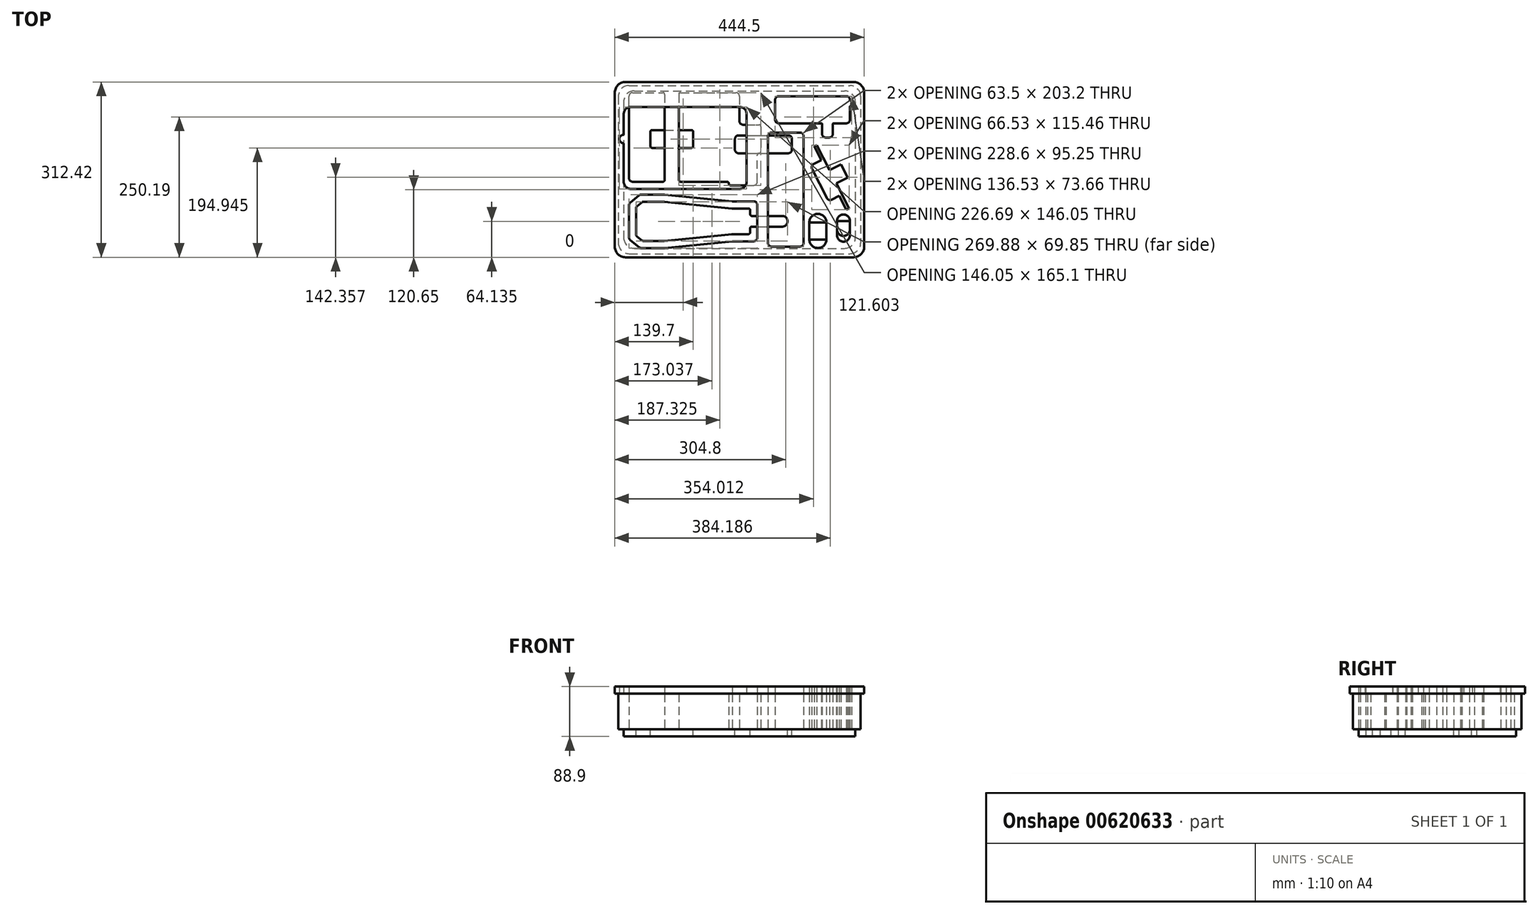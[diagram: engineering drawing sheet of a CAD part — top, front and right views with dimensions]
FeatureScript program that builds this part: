
annotation { "Feature Type Name" : "Feature", "Feature Type Description" : "" }
export const myFeature = defineFeature(function(context is Context, id is Id, definition is map)
    precondition{}
    {
        {
            var Q0;
            Q0=qCreatedBy(makeId("Top.planeOp"),FACE);
            var sketch = newSketch(context, id + "F0", { "sketchPlane" : qUnion([Q0])});
            skLineSegment(sketch, "E0.bottom", {"start": v(-196.85, 149.86) * mm, "end": v(196.85, 149.86) * mm});
            skLineSegment(sketch, "E0.top", {"start": v(-196.85, -149.86) * mm, "end": v(196.85, -149.86) * mm});
            skLineSegment(sketch, "E0.left", {"start": v(-215.9, 130.81) * mm, "end": v(-215.9, -130.81) * mm});
            skLineSegment(sketch, "E0.right", {"start": v(215.9, 130.81) * mm, "end": v(215.9, -130.8) * mm});
            skLineSegment(sketch, "E1.bottom", {"start": v(-196.85, -15.24) * mm, "end": v(-196.85, 130.81) * mm});
            skLineSegment(sketch, "E1.top", {"start": v(31.75, -21.59) * mm, "end": v(31.75, 26.04) * mm});
            skLineSegment(sketch, "E1.right", {"start": v(-190.5, 137.16) * mm, "end": v(-136.52, 137.16) * mm});
            skLineSegment(sketch, "E2.bottom", {"start": v(124.46, -93.98) * mm, "end": v(154.94, -93.98) * mm});
            skLineSegment(sketch, "E2.top", {"start": v(124.46, -124.46) * mm, "end": v(154.94, -124.46) * mm});
            skLineSegment(sketch, "E2.left", {"start": v(124.46, -93.98) * mm, "end": v(124.46, -124.46) * mm});
            skLineSegment(sketch, "E2.right", {"start": v(154.94, -93.98) * mm, "end": v(154.94, -124.46) * mm});
            skLineSegment(sketch, "E3", {"start": v(142.6, -24.8) * mm, "end": v(186.74, -2.32) * mm, "construction": true});
            skLineSegment(sketch, "E4", {"start": v(142.6, -24.8) * mm, "end": v(155.87, -50.83) * mm});
            skLineSegment(sketch, "E5", {"start": v(164.4, -53.6) * mm, "end": v(177.99, -46.7) * mm});
            skLineSegment(sketch, "E6", {"start": v(177.99, -46.7) * mm, "end": v(190.67, -71.59) * mm});
            skLineSegment(sketch, "E7", {"start": v(190.67, -71.59) * mm, "end": v(195.2, -69.28) * mm});
            skLineSegment(sketch, "E8", {"start": v(160.32, -0.82) * mm, "end": v(180.68, 9.56) * mm});
            skLineSegment(sketch, "E9", {"start": v(180.68, 9.56) * mm, "end": v(186.74, -2.32) * mm});
            skPoint(sketch, "E10.visualSharp", {"position": v(158.75, -56.5) * mm});
            skArc(sketch, "E10.filletArc", {"start": v(155.87, -50.83) * mm, "mid": v(159.56, -54) * mm, "end": v(164.4, -53.6) * mm});
            skArc(sketch, "E11.MirrorCS", {"start": v(129.35, 1.22) * mm, "mid": v(128.96, 6.06) * mm, "end": v(132.12, 9.76) * mm});
            skLineSegment(sketch, "E12.MirrorCS", {"start": v(145.7, 16.68) * mm, "end": v(133.02, 41.57) * mm});
            skLineSegment(sketch, "E13.MirrorCS", {"start": v(132.12, 9.76) * mm, "end": v(145.7, 16.68) * mm});
            skPoint(sketch, "E14.MirrorP", {"position": v(126.46, 6.88) * mm});
            skLineSegment(sketch, "E15.MirrorCS", {"start": v(172.42, -24.58) * mm, "end": v(192.8, -14.2) * mm});
            skLineSegment(sketch, "E16.MirrorCS", {"start": v(142.6, -24.8) * mm, "end": v(129.35, 1.22) * mm});
            skLineSegment(sketch, "E17.MirrorCS", {"start": v(192.8, -14.2) * mm, "end": v(186.74, -2.32) * mm});
            skLineSegment(sketch, "E18", {"start": v(172.42, -24.58) * mm, "end": v(195.2, -69.28) * mm});
            skPoint(sketch, "E19.visualSharp", {"position": v(-215.9, 149.86) * mm});
            skArc(sketch, "E19.filletArc", {"start": v(-196.85, 149.86) * mm, "mid": v(-210.32, 144.28) * mm, "end": v(-215.9, 130.81) * mm});
            skPoint(sketch, "E20.visualSharp", {"position": v(215.9, 149.86) * mm});
            skArc(sketch, "E20.filletArc", {"start": v(215.9, 130.81) * mm, "mid": v(210.32, 144.28) * mm, "end": v(196.85, 149.86) * mm});
            skPoint(sketch, "E21.visualSharp", {"position": v(215.9, -149.86) * mm});
            skArc(sketch, "E21.filletArc", {"start": v(196.85, -149.86) * mm, "mid": v(210.32, -144.28) * mm, "end": v(215.9, -130.8) * mm});
            skPoint(sketch, "E22.visualSharp", {"position": v(-215.9, -149.86) * mm});
            skArc(sketch, "E22.filletArc", {"start": v(-215.9, -130.81) * mm, "mid": v(-210.32, -144.28) * mm, "end": v(-196.85, -149.86) * mm});
            skPoint(sketch, "E23.visualSharp", {"position": v(-196.85, -27.94) * mm});
            skPoint(sketch, "E24.visualSharp", {"position": v(31.75, -27.94) * mm});
            skArc(sketch, "E24.filletArc", {"start": v(25.4, -27.94) * mm, "mid": v(29.9, -26.08) * mm, "end": v(31.75, -21.59) * mm});
            skPoint(sketch, "E25.visualSharp", {"position": v(-196.85, 137.16) * mm});
            skArc(sketch, "E25.filletArc", {"start": v(-190.5, 137.16) * mm, "mid": v(-195, 135.3) * mm, "end": v(-196.85, 130.81) * mm});
            skPoint(sketch, "E26.visualSharp", {"position": v(31.75, 137.16) * mm});
            skArc(sketch, "E26.filletArc", {"start": v(31.75, 130.81) * mm, "mid": v(29.9, 135.3) * mm, "end": v(25.4, 137.16) * mm, "construction": true});
            skLineSegment(sketch, "E27.bottom", {"start": v(63.5, 88.9) * mm, "end": v(63.5, 124.46) * mm});
            skLineSegment(sketch, "E27.top", {"start": v(196.85, 88.9) * mm, "end": v(196.85, 112.08) * mm});
            skLineSegment(sketch, "E27.left", {"start": v(69.85, 82.55) * mm, "end": v(146.05, 82.55) * mm});
            skLineSegment(sketch, "E27.right", {"start": v(69.85, 130.81) * mm, "end": v(190.5, 130.81) * mm});
            skLineSegment(sketch, "E28.bottom", {"start": v(147.32, 81.28) * mm, "end": v(147.32, 63.5) * mm});
            skLineSegment(sketch, "E28.top", {"start": v(166.37, 81.28) * mm, "end": v(166.37, 63.5) * mm});
            skLineSegment(sketch, "E28.right", {"start": v(153.67, 57.15) * mm, "end": v(160.02, 57.15) * mm});
            skLineSegment(sketch, "E29.trimOffspring", {"start": v(167.64, 82.55) * mm, "end": v(190.5, 82.55) * mm});
            skLineSegment(sketch, "E30", {"start": v(147.32, 82.55) * mm, "end": v(166.37, 82.55) * mm, "construction": true});
            skPoint(sketch, "E31.visualSharp", {"position": v(63.5, 82.55) * mm});
            skArc(sketch, "E31.filletArc", {"start": v(63.5, 88.9) * mm, "mid": v(65.36, 84.4) * mm, "end": v(69.85, 82.55) * mm});
            skPoint(sketch, "E32.visualSharp", {"position": v(196.85, 82.55) * mm});
            skArc(sketch, "E32.filletArc", {"start": v(190.5, 82.55) * mm, "mid": v(195, 84.4) * mm, "end": v(196.85, 88.9) * mm});
            skArc(sketch, "E33.filletArc", {"start": v(196.85, 124.46) * mm, "mid": v(195, 128.95) * mm, "end": v(190.5, 130.81) * mm});
            skPoint(sketch, "E34.visualSharp", {"position": v(63.5, 130.81) * mm});
            skArc(sketch, "E34.filletArc", {"start": v(69.85, 130.81) * mm, "mid": v(65.36, 128.95) * mm, "end": v(63.5, 124.46) * mm});
            skPoint(sketch, "E35.visualSharp", {"position": v(147.32, 57.15) * mm});
            skArc(sketch, "E35.filletArc", {"start": v(147.32, 63.5) * mm, "mid": v(149.18, 59) * mm, "end": v(153.67, 57.15) * mm});
            skPoint(sketch, "E36.visualSharp", {"position": v(166.37, 57.15) * mm});
            skArc(sketch, "E36.filletArc", {"start": v(160.02, 57.15) * mm, "mid": v(164.51, 59) * mm, "end": v(166.37, 63.5) * mm});
            skLineSegment(sketch, "E37.bottom", {"start": v(173.74, -91.44) * mm, "end": v(196.85, -91.44) * mm});
            skLineSegment(sketch, "E37.left", {"start": v(173.74, -91.44) * mm, "end": v(173.74, -106.68) * mm});
            skLineSegment(sketch, "E37.right", {"start": v(196.85, -91.44) * mm, "end": v(196.85, -106.68) * mm});
            skArc(sketch, "E38", {"start": v(173.74, -106.68) * mm, "mid": v(185.3, -118.24) * mm, "end": v(196.85, -106.68) * mm});
            skLineSegment(sketch, "E39.bottom", {"start": v(-196.85, -139.7) * mm, "end": v(-196.85, -44.45) * mm, "construction": true});
            skLineSegment(sketch, "E39.top", {"start": v(31.75, -139.7) * mm, "end": v(31.75, -44.45) * mm, "construction": true});
            skLineSegment(sketch, "E39.left", {"start": v(-196.85, -139.7) * mm, "end": v(31.75, -139.7) * mm, "construction": true});
            skLineSegment(sketch, "E39.right", {"start": v(-196.85, -44.45) * mm, "end": v(31.75, -44.45) * mm, "construction": true});
            skLineSegment(sketch, "E40", {"start": v(-196.85, -92.08) * mm, "end": v(31.75, -92.07) * mm, "construction": true});
            skLineSegment(sketch, "E41", {"start": v(-196.85, -123.83) * mm, "end": v(31.75, -123.82) * mm, "construction": true});
            skLineSegment(sketch, "E42.MirrorCS", {"start": v(-196.85, -60.33) * mm, "end": v(31.75, -60.32) * mm, "construction": true});
            skLineSegment(sketch, "E43", {"start": v(-196.85, -127.64) * mm, "end": v(31.75, -127.63) * mm, "construction": true});
            skLineSegment(sketch, "E44.MirrorCS", {"start": v(-196.85, -56.51) * mm, "end": v(31.75, -56.51) * mm, "construction": true});
            skLineSegment(sketch, "E45", {"start": v(-177.16, -139.7) * mm, "end": v(-177.16, -44.45) * mm, "construction": true});
            skLineSegment(sketch, "E46", {"start": v(-133.35, -139.7) * mm, "end": v(-133.35, -44.45) * mm, "construction": true});
            skLineSegment(sketch, "E47", {"start": v(-12.7, -139.7) * mm, "end": v(-12.7, -44.45) * mm, "construction": true});
            skLineSegment(sketch, "E48", {"start": v(-196.85, -120.79) * mm, "end": v(-196.85, -63.36) * mm});
            skLineSegment(sketch, "E49", {"start": v(-194.49, -58.42) * mm, "end": v(-178.9, -45.86) * mm});
            skLineSegment(sketch, "E50", {"start": v(-174.92, -44.45) * mm, "end": v(-133.35, -44.45) * mm});
            skLineSegment(sketch, "E51", {"start": v(-133.35, -44.45) * mm, "end": v(-12.7, -56.51) * mm});
            skLineSegment(sketch, "E52", {"start": v(-12.7, -56.51) * mm, "end": v(25.4, -56.51) * mm});
            skLineSegment(sketch, "E53", {"start": v(31.75, -62.86) * mm, "end": v(31.75, -121.28) * mm});
            skLineSegment(sketch, "E54", {"start": v(25.4, -127.63) * mm, "end": v(-12.7, -127.63) * mm});
            skLineSegment(sketch, "E55", {"start": v(-12.7, -127.64) * mm, "end": v(-133.35, -139.7) * mm});
            skLineSegment(sketch, "E56", {"start": v(-133.35, -139.7) * mm, "end": v(-174.92, -139.7) * mm});
            skLineSegment(sketch, "E57", {"start": v(-178.9, -138.3) * mm, "end": v(-194.49, -125.73) * mm});
            skPoint(sketch, "E58.visualSharp", {"position": v(31.75, -127.64) * mm});
            skArc(sketch, "E58.filletArc", {"start": v(25.4, -127.63) * mm, "mid": v(29.9, -125.78) * mm, "end": v(31.75, -121.28) * mm});
            skPoint(sketch, "E59.visualSharp", {"position": v(31.75, -56.51) * mm});
            skArc(sketch, "E59.filletArc", {"start": v(31.75, -62.86) * mm, "mid": v(29.9, -58.37) * mm, "end": v(25.4, -56.51) * mm});
            skPoint(sketch, "E60.visualSharp", {"position": v(-196.85, -123.83) * mm});
            skArc(sketch, "E60.filletArc", {"start": v(-196.85, -120.79) * mm, "mid": v(-196.23, -123.53) * mm, "end": v(-194.49, -125.73) * mm});
            skPoint(sketch, "E61.visualSharp", {"position": v(-177.16, -139.7) * mm});
            skArc(sketch, "E61.filletArc", {"start": v(-178.9, -138.3) * mm, "mid": v(-177.04, -139.34) * mm, "end": v(-174.92, -139.7) * mm});
            skPoint(sketch, "E62.visualSharp", {"position": v(-196.85, -60.33) * mm});
            skArc(sketch, "E62.filletArc", {"start": v(-194.49, -58.42) * mm, "mid": v(-196.23, -60.62) * mm, "end": v(-196.85, -63.36) * mm});
            skPoint(sketch, "E63.visualSharp", {"position": v(-177.16, -44.45) * mm});
            skArc(sketch, "E63.filletArc", {"start": v(-174.92, -44.45) * mm, "mid": v(-177.04, -44.81) * mm, "end": v(-178.9, -45.86) * mm});
            skLineSegment(sketch, "E64", {"start": v(173.74, -106.68) * mm, "end": v(196.85, -106.68) * mm, "construction": true});
            skLineSegment(sketch, "E65.MirrorCS", {"start": v(160.32, -0.82) * mm, "end": v(137.54, 43.88) * mm});
            skLineSegment(sketch, "E66.MirrorCS", {"start": v(133.02, 41.57) * mm, "end": v(137.54, 43.88) * mm});
            skLineSegment(sketch, "E67", {"start": v(198.12, 122.87) * mm, "end": v(198.76, 122.87) * mm});
            skLineSegment(sketch, "E68", {"start": v(200.02, 121.6) * mm, "end": v(200.02, 114.62) * mm});
            skLineSegment(sketch, "E69", {"start": v(198.76, 113.35) * mm, "end": v(198.12, 113.35) * mm});
            skPoint(sketch, "E70.visualSharp", {"position": v(166.37, 82.55) * mm});
            skArc(sketch, "E70.filletArc", {"start": v(167.64, 82.55) * mm, "mid": v(166.74, 82.18) * mm, "end": v(166.37, 81.28) * mm});
            skPoint(sketch, "E71.visualSharp", {"position": v(147.32, 82.55) * mm});
            skArc(sketch, "E71.filletArc", {"start": v(147.32, 81.28) * mm, "mid": v(146.95, 82.18) * mm, "end": v(146.05, 82.55) * mm});
            skPoint(sketch, "E72.visualSharp", {"position": v(200.03, 113.35) * mm});
            skArc(sketch, "E72.filletArc", {"start": v(198.76, 113.35) * mm, "mid": v(199.65, 113.72) * mm, "end": v(200.03, 114.62) * mm});
            skPoint(sketch, "E73.visualSharp", {"position": v(200.03, 122.87) * mm});
            skArc(sketch, "E73.filletArc", {"start": v(200.02, 121.6) * mm, "mid": v(199.65, 122.5) * mm, "end": v(198.76, 122.87) * mm});
            skPoint(sketch, "E74.visualSharp", {"position": v(196.85, 122.87) * mm});
            skArc(sketch, "E74.filletArc", {"start": v(196.85, 124.13) * mm, "mid": v(197.23, 123.24) * mm, "end": v(198.12, 122.87) * mm});
            skPoint(sketch, "E75.visualSharp", {"position": v(196.85, 113.35) * mm});
            skArc(sketch, "E75.filletArc", {"start": v(198.12, 113.35) * mm, "mid": v(197.22, 112.98) * mm, "end": v(196.85, 112.08) * mm});
            skLineSegment(sketch, "E76", {"start": v(-196.85, 54.61) * mm, "end": v(31.75, 54.61) * mm, "construction": true});
            skLineSegment(sketch, "E77", {"start": v(-82.55, -27.94) * mm, "end": v(-82.55, 137.16) * mm, "construction": true});
            skLineSegment(sketch, "E78", {"start": v(0, 149.86) * mm, "end": v(0, -149.86) * mm, "construction": true});
            skLineSegment(sketch, "E79", {"start": v(-215.9, 0) * mm, "end": v(215.9, 0) * mm, "construction": true});
            skPoint(sketch, "E80", {"position": v(0, 0) * mm});
            skPoint(sketch, "E81", {"position": v(-82.55, 54.61) * mm});
            skPoint(sketch, "E82", {"position": v(-133.35, -92.08) * mm});
            skLineSegment(sketch, "E83", {"start": v(63.5, 106.68) * mm, "end": v(196.85, 106.68) * mm, "construction": true});
            skLineSegment(sketch, "E84", {"start": v(130.18, 130.81) * mm, "end": v(130.18, 82.55) * mm, "construction": true});
            skPoint(sketch, "E85", {"position": v(130.18, 106.68) * mm});
            skLineSegment(sketch, "E86", {"start": v(172.42, -24.58) * mm, "end": v(160.32, -0.82) * mm, "construction": true});
            skPoint(sketch, "E87", {"position": v(166.37, -12.7) * mm});
            skLineSegment(sketch, "E88", {"start": v(196.85, 124.46) * mm, "end": v(196.85, 124.13) * mm});
            skLineSegment(sketch, "E89", {"start": v(196.85, 124.13) * mm, "end": v(196.85, 112.08) * mm, "construction": true});
            skArc(sketch, "E90", {"start": v(31.75, -21.59) * mm, "mid": v(29.9, -26.08) * mm, "end": v(25.4, -27.94) * mm});
            skLineSegment(sketch, "E91.bottom", {"start": v(107.95, -137.16) * mm, "end": v(57.15, -137.16) * mm});
            skLineSegment(sketch, "E91.top", {"start": v(107.95, 66.04) * mm, "end": v(57.15, 66.04) * mm});
            skLineSegment(sketch, "E91.left", {"start": v(114.3, -130.8) * mm, "end": v(114.3, 59.7) * mm});
            skLineSegment(sketch, "E91.right", {"start": v(50.8, -130.8) * mm, "end": v(50.8, 59.7) * mm});
            skLineSegment(sketch, "E92", {"start": v(82.55, -137.16) * mm, "end": v(82.55, 66.04) * mm, "construction": true});
            skLineSegment(sketch, "E93", {"start": v(114.3, -35.56) * mm, "end": v(50.8, -35.56) * mm, "construction": true});
            skPoint(sketch, "E94", {"position": v(82.55, -35.56) * mm});
            skPoint(sketch, "E95.visualSharp", {"position": v(114.3, -137.16) * mm});
            skArc(sketch, "E95.filletArc", {"start": v(107.95, -137.16) * mm, "mid": v(112.44, -135.3) * mm, "end": v(114.3, -130.8) * mm});
            skPoint(sketch, "E96.visualSharp", {"position": v(50.8, -137.16) * mm});
            skArc(sketch, "E96.filletArc", {"start": v(50.8, -130.8) * mm, "mid": v(52.66, -135.3) * mm, "end": v(57.15, -137.16) * mm});
            skPoint(sketch, "E97.visualSharp", {"position": v(50.8, 66.04) * mm});
            skArc(sketch, "E97.filletArc", {"start": v(57.15, 66.04) * mm, "mid": v(52.66, 64.18) * mm, "end": v(50.8, 59.7) * mm});
            skPoint(sketch, "E98.visualSharp", {"position": v(114.3, 66.04) * mm});
            skArc(sketch, "E98.filletArc", {"start": v(114.3, 59.7) * mm, "mid": v(112.44, 64.18) * mm, "end": v(107.95, 66.04) * mm});
            skLineSegment(sketch, "E99.left", {"start": v(-107.95, 133.99) * mm, "end": v(-107.95, -18.41) * mm});
            skLineSegment(sketch, "E99.right", {"start": v(-133.35, 133.99) * mm, "end": v(-133.35, -18.41) * mm});
            skLineSegment(sketch, "E100", {"start": v(34.93, 80.01) * mm, "end": v(34.92, 80.01) * mm});
            skLineSegment(sketch, "E101.MirrorCS", {"start": v(34.93, 29.21) * mm, "end": v(34.93, 29.21) * mm});
            skLineSegment(sketch, "E102", {"start": v(38.1, 76.84) * mm, "end": v(38.1, 32.39) * mm});
            skLineSegment(sketch, "E103", {"start": v(-104.77, 137.16) * mm, "end": v(-6.35, 137.16) * mm});
            skLineSegment(sketch, "E104", {"start": v(31.75, 83.19) * mm, "end": v(31.75, 130.81) * mm, "construction": true});
            skLineSegment(sketch, "E105", {"start": v(31.75, 29.21) * mm, "end": v(31.75, 80.01) * mm, "construction": true});
            skLineSegment(sketch, "E106", {"start": v(-133.35, 137.16) * mm, "end": v(-107.95, 137.16) * mm, "construction": true});
            skPoint(sketch, "E107.visualSharp", {"position": v(-107.95, 137.16) * mm});
            skArc(sketch, "E107.filletArc", {"start": v(-104.77, 137.16) * mm, "mid": v(-107.02, 136.23) * mm, "end": v(-107.95, 133.99) * mm});
            skPoint(sketch, "E108.visualSharp", {"position": v(-133.35, 137.16) * mm});
            skArc(sketch, "E108.filletArc", {"start": v(-133.35, 133.99) * mm, "mid": v(-134.28, 136.23) * mm, "end": v(-136.52, 137.16) * mm});
            skPoint(sketch, "E109.visualSharp", {"position": v(31.75, 80.01) * mm});
            skPoint(sketch, "E110.visualSharp", {"position": v(31.75, 29.21) * mm});
            skArc(sketch, "E110.filletArc", {"start": v(34.93, 29.21) * mm, "mid": v(32.68, 28.28) * mm, "end": v(31.75, 26.04) * mm});
            skPoint(sketch, "E111.visualSharp", {"position": v(38.1, 29.21) * mm});
            skArc(sketch, "E111.filletArc", {"start": v(34.93, 29.21) * mm, "mid": v(37.17, 30.14) * mm, "end": v(38.1, 32.39) * mm});
            skPoint(sketch, "E112.visualSharp", {"position": v(38.1, 80.01) * mm});
            skArc(sketch, "E112.filletArc", {"start": v(38.1, 76.84) * mm, "mid": v(37.17, 79.08) * mm, "end": v(34.92, 80.01) * mm});
            skLineSegment(sketch, "E113", {"start": v(0, 130.81) * mm, "end": v(0, 86.36) * mm});
            skLineSegment(sketch, "E114", {"start": v(6.35, 80.01) * mm, "end": v(34.93, 80.01) * mm});
            skPoint(sketch, "E115.visualSharp", {"position": v(0, 80.01) * mm});
            skArc(sketch, "E115.filletArc", {"start": v(0, 86.36) * mm, "mid": v(1.86, 81.87) * mm, "end": v(6.35, 80.01) * mm});
            skLineSegment(sketch, "E116", {"start": v(-6.35, 137.16) * mm, "end": v(0, 137.16) * mm, "construction": true});
            skLineSegment(sketch, "E117", {"start": v(0, 137.16) * mm, "end": v(25.4, 137.16) * mm, "construction": true});
            skPoint(sketch, "E118.visualSharp", {"position": v(0, 137.16) * mm});
            skArc(sketch, "E118.filletArc", {"start": v(0, 130.81) * mm, "mid": v(-1.86, 135.3) * mm, "end": v(-6.35, 137.16) * mm});
            skLineSegment(sketch, "E119", {"start": v(-6.35, 137.16) * mm, "end": v(-6.35, 137.16) * mm});
            skLineSegment(sketch, "E120", {"start": v(-19.05, -24.76) * mm, "end": v(-19.05, -24.76) * mm});
            skLineSegment(sketch, "E121", {"start": v(-22.22, -21.59) * mm, "end": v(-104.78, -21.59) * mm});
            skLineSegment(sketch, "E122", {"start": v(-133.35, -21.59) * mm, "end": v(-133.35, -24.76) * mm, "construction": true});
            skLineSegment(sketch, "E123", {"start": v(-15.88, -27.94) * mm, "end": v(25.4, -27.94) * mm});
            skLineSegment(sketch, "E124", {"start": v(-107.95, -21.59) * mm, "end": v(-107.95, -24.76) * mm, "construction": true});
            skPoint(sketch, "E125.visualSharp", {"position": v(-196.85, -21.59) * mm});
            skArc(sketch, "E125.filletArc", {"start": v(-196.85, -15.24) * mm, "mid": v(-195, -19.73) * mm, "end": v(-190.5, -21.59) * mm});
            skPoint(sketch, "E126.visualSharp", {"position": v(-19.05, -21.59) * mm});
            skArc(sketch, "E126.filletArc", {"start": v(-19.05, -24.76) * mm, "mid": v(-19.98, -22.52) * mm, "end": v(-22.22, -21.59) * mm});
            skPoint(sketch, "E127.visualSharp", {"position": v(-19.05, -27.94) * mm});
            skArc(sketch, "E127.filletArc", {"start": v(-19.05, -24.76) * mm, "mid": v(-18.12, -27.01) * mm, "end": v(-15.88, -27.94) * mm});
            skLineSegment(sketch, "E128", {"start": v(-136.53, -21.59) * mm, "end": v(-190.5, -21.59) * mm});
            skPoint(sketch, "E129.visualSharp", {"position": v(-133.35, -21.59) * mm});
            skArc(sketch, "E129.filletArc", {"start": v(-136.53, -21.59) * mm, "mid": v(-134.28, -20.66) * mm, "end": v(-133.35, -18.41) * mm});
            skPoint(sketch, "E130.visualSharp", {"position": v(-107.95, -21.59) * mm});
            skArc(sketch, "E130.filletArc", {"start": v(-107.95, -18.41) * mm, "mid": v(-107.02, -20.66) * mm, "end": v(-104.78, -21.59) * mm});
            skSolve(sketch);
        }
        {
            var Q0;
            Q0=qSketchRegion(id+"F0",true);
            extrude(context, id + "F1", {"entities" : qUnion([Q0]), "depth" : 63.5 * mm, "offsetDistance" : 25.4 * mm});
        }
        {
            var Q0;
            Q0=qCreatedBy(makeId("Top.planeOp"),FACE);
            var sketch = newSketch(context, id + "F2", { "sketchPlane" : qUnion([Q0])});
            skLineSegment(sketch, "E131.0", {"start": v(-215.9, 149.86) * mm, "end": v(215.9, 149.86) * mm, "construction": true});
            skLineSegment(sketch, "E132.0", {"start": v(-215.9, 149.86) * mm, "end": v(-215.9, -149.86) * mm, "construction": true});
            skLineSegment(sketch, "E133.0", {"start": v(215.9, 149.86) * mm, "end": v(215.9, -149.86) * mm, "construction": true});
            skLineSegment(sketch, "E134.0", {"start": v(-190.26, -149.86) * mm, "end": v(215.9, -149.86) * mm, "construction": true});
            skPoint(sketch, "E135.orphan", {"position": v(-196.85, 149.86) * mm});
            skPoint(sketch, "E136.orphan", {"position": v(-215.9, 130.81) * mm});
            skPoint(sketch, "E137.orphan", {"position": v(196.85, 149.86) * mm});
            skPoint(sketch, "E138.orphan", {"position": v(215.9, 130.81) * mm});
            skPoint(sketch, "E139.orphan", {"position": v(215.9, -130.8) * mm});
            skPoint(sketch, "E140.orphan", {"position": v(196.85, -149.86) * mm});
            skPoint(sketch, "E141.orphan", {"position": v(-196.85, -149.86) * mm});
            skPoint(sketch, "E142.orphan", {"position": v(-215.9, -130.81) * mm});
            skPoint(sketch, "E143", {"position": v(0, 0) * mm});
            skLineSegment(sketch, "E144", {"start": v(0, 149.86) * mm, "end": v(0, -149.86) * mm, "construction": true});
            skPoint(sketch, "E144.startSnap0", {"position": v(0, 149.86) * mm});
            skLineSegment(sketch, "E145", {"start": v(-215.9, 0) * mm, "end": v(215.9, 0) * mm, "construction": true});
            skLineSegment(sketch, "E146.bottom", {"start": v(-187.32, 140.34) * mm, "end": v(187.33, 140.34) * mm});
            skLineSegment(sketch, "E146.top", {"start": v(-187.33, -140.33) * mm, "end": v(187.32, -140.33) * mm});
            skLineSegment(sketch, "E146.left", {"start": v(-206.38, 121.29) * mm, "end": v(-206.38, -121.28) * mm});
            skLineSegment(sketch, "E146.right", {"start": v(206.38, 121.29) * mm, "end": v(206.38, -121.28) * mm});
            skPoint(sketch, "E147.visualSharp", {"position": v(-206.38, 140.34) * mm});
            skPoint(sketch, "E148.visualSharp", {"position": v(206.38, 140.34) * mm});
            skPoint(sketch, "E149.visualSharp", {"position": v(206.38, -140.33) * mm});
            skPoint(sketch, "E150.visualSharp", {"position": v(-206.38, -140.33) * mm});
            skLineSegment(sketch, "E151.0.0", {"start": v(-12.7, -127.63) * mm, "end": v(25.4, -127.63) * mm, "construction": true});
            skArc(sketch, "E151.0.1", {"start": v(25.4, -127.63) * mm, "mid": v(29.9, -125.78) * mm, "end": v(31.75, -121.28) * mm, "construction": true});
            skLineSegment(sketch, "E151.0.2", {"start": v(31.75, -121.28) * mm, "end": v(31.75, -62.86) * mm, "construction": true});
            skArc(sketch, "E151.0.3", {"start": v(31.75, -62.86) * mm, "mid": v(29.9, -58.37) * mm, "end": v(25.4, -56.51) * mm, "construction": true});
            skLineSegment(sketch, "E151.0.4", {"start": v(25.4, -56.51) * mm, "end": v(-12.7, -56.51) * mm, "construction": true});
            skLineSegment(sketch, "E151.0.5", {"start": v(-12.7, -56.52) * mm, "end": v(-133.35, -44.45) * mm, "construction": true});
            skLineSegment(sketch, "E151.0.6", {"start": v(-133.35, -44.45) * mm, "end": v(-174.92, -44.45) * mm, "construction": true});
            skArc(sketch, "E151.0.7", {"start": v(-174.92, -44.45) * mm, "mid": v(-177.04, -44.81) * mm, "end": v(-178.9, -45.86) * mm, "construction": true});
            skLineSegment(sketch, "E151.0.8", {"start": v(-178.9, -45.86) * mm, "end": v(-194.49, -58.42) * mm, "construction": true});
            skArc(sketch, "E151.0.9", {"start": v(-194.49, -58.42) * mm, "mid": v(-196.23, -60.62) * mm, "end": v(-196.85, -63.36) * mm, "construction": true});
            skLineSegment(sketch, "E151.0.10", {"start": v(-196.85, -63.36) * mm, "end": v(-196.85, -120.79) * mm, "construction": true});
            skArc(sketch, "E151.0.11", {"start": v(-196.85, -120.79) * mm, "mid": v(-196.23, -123.53) * mm, "end": v(-194.49, -125.73) * mm, "construction": true});
            skLineSegment(sketch, "E151.0.12", {"start": v(-194.49, -125.73) * mm, "end": v(-178.9, -138.3) * mm, "construction": true});
            skArc(sketch, "E151.0.13", {"start": v(-178.9, -138.3) * mm, "mid": v(-177.04, -139.34) * mm, "end": v(-174.92, -139.7) * mm, "construction": true});
            skLineSegment(sketch, "E151.0.14", {"start": v(-174.92, -139.7) * mm, "end": v(-133.35, -139.7) * mm, "construction": true});
            skLineSegment(sketch, "E151.0.15", {"start": v(-133.35, -139.7) * mm, "end": v(-12.7, -127.64) * mm, "construction": true});
            skArc(sketch, "E152.filletArc", {"start": v(-187.32, 140.34) * mm, "mid": v(-200.8, 134.76) * mm, "end": v(-206.38, 121.29) * mm});
            skArc(sketch, "E153.filletArc", {"start": v(206.38, 121.29) * mm, "mid": v(200.8, 134.76) * mm, "end": v(187.33, 140.34) * mm});
            skArc(sketch, "E154.filletArc", {"start": v(187.32, -140.33) * mm, "mid": v(200.8, -134.76) * mm, "end": v(206.37, -121.28) * mm});
            skArc(sketch, "E155.filletArc", {"start": v(-206.38, -121.28) * mm, "mid": v(-200.8, -134.76) * mm, "end": v(-187.33, -140.33) * mm});
            skLineSegment(sketch, "E156.0", {"start": v(-173.55, -57.85) * mm, "end": v(-182.97, -65.45) * mm});
            skLineSegment(sketch, "E156.1", {"start": v(-134.14, -57.15) * mm, "end": v(-171.56, -57.15) * mm});
            skLineSegment(sketch, "E156.2", {"start": v(-184.15, -67.92) * mm, "end": v(-184.15, -116.23) * mm});
            skLineSegment(sketch, "E156.3", {"start": v(-13.5, -69.2) * mm, "end": v(-133.83, -57.17) * mm});
            skLineSegment(sketch, "E156.4", {"start": v(15.88, -69.21) * mm, "end": v(-13.18, -69.21) * mm});
            skLineSegment(sketch, "E156.5", {"start": v(19.05, -111.76) * mm, "end": v(19.05, -104.78) * mm});
            skLineSegment(sketch, "E156.6", {"start": v(-182.97, -118.7) * mm, "end": v(-173.55, -126.3) * mm});
            skLineSegment(sketch, "E156.7", {"start": v(-171.56, -127) * mm, "end": v(-134.14, -127) * mm});
            skLineSegment(sketch, "E156.8", {"start": v(-133.83, -126.98) * mm, "end": v(-13.5, -114.95) * mm});
            skLineSegment(sketch, "E156.9", {"start": v(-13.18, -114.93) * mm, "end": v(15.88, -114.93) * mm});
            skLineSegment(sketch, "E157", {"start": v(22.23, -82.55) * mm, "end": v(76.2, -82.55) * mm});
            skLineSegment(sketch, "E158", {"start": v(-184.15, -92.08) * mm, "end": v(76.2, -92.08) * mm, "construction": true});
            skLineSegment(sketch, "E159", {"start": v(76.2, -82.55) * mm, "end": v(76.2, -92.08) * mm, "construction": true});
            skLineSegment(sketch, "E160.MirrorCS", {"start": v(22.23, -101.6) * mm, "end": v(76.2, -101.6) * mm});
            skLineSegment(sketch, "E161.MirrorCS", {"start": v(76.2, -101.6) * mm, "end": v(76.2, -92.08) * mm, "construction": true});
            skLineSegment(sketch, "E162", {"start": v(19.05, -79.37) * mm, "end": v(19.05, -72.39) * mm});
            skPoint(sketch, "E163.orphan", {"position": v(19.05, -92.08) * mm});
            skArc(sketch, "E164", {"start": v(76.2, -82.55) * mm, "mid": v(85.73, -92.08) * mm, "end": v(76.2, -101.6) * mm});
            skLineSegment(sketch, "E165.bottom", {"start": v(-1.78, 60.96) * mm, "end": v(87.12, 60.96) * mm});
            skLineSegment(sketch, "E165.top", {"start": v(-1.78, 29.21) * mm, "end": v(87.12, 29.21) * mm});
            skLineSegment(sketch, "E165.left", {"start": v(-8.13, 54.61) * mm, "end": v(-8.13, 35.56) * mm});
            skLineSegment(sketch, "E165.right", {"start": v(93.47, 54.61) * mm, "end": v(93.47, 35.56) * mm});
            skPoint(sketch, "E166.visualSharp", {"position": v(-8.13, 60.96) * mm});
            skArc(sketch, "E166.filletArc", {"start": v(-1.78, 60.96) * mm, "mid": v(-6.27, 59.1) * mm, "end": v(-8.13, 54.61) * mm});
            skPoint(sketch, "E167.visualSharp", {"position": v(93.47, 60.96) * mm});
            skArc(sketch, "E167.filletArc", {"start": v(93.47, 54.61) * mm, "mid": v(91.61, 59.1) * mm, "end": v(87.12, 60.96) * mm});
            skPoint(sketch, "E168.visualSharp", {"position": v(93.47, 29.21) * mm});
            skArc(sketch, "E168.filletArc", {"start": v(87.12, 29.21) * mm, "mid": v(91.61, 31.07) * mm, "end": v(93.47, 35.56) * mm});
            skPoint(sketch, "E169.visualSharp", {"position": v(-8.13, 29.21) * mm});
            skArc(sketch, "E169.filletArc", {"start": v(-8.13, 35.56) * mm, "mid": v(-6.27, 31.07) * mm, "end": v(-1.78, 29.21) * mm});
            skPoint(sketch, "E170.visualSharp", {"position": v(19.05, -69.21) * mm});
            skArc(sketch, "E170.filletArc", {"start": v(19.05, -72.39) * mm, "mid": v(18.12, -70.14) * mm, "end": v(15.88, -69.21) * mm});
            skPoint(sketch, "E171.visualSharp", {"position": v(19.05, -82.55) * mm});
            skArc(sketch, "E171.filletArc", {"start": v(19.05, -79.37) * mm, "mid": v(19.98, -81.62) * mm, "end": v(22.23, -82.55) * mm});
            skPoint(sketch, "E172.visualSharp", {"position": v(19.05, -101.6) * mm});
            skArc(sketch, "E172.filletArc", {"start": v(22.23, -101.6) * mm, "mid": v(19.98, -102.53) * mm, "end": v(19.05, -104.78) * mm});
            skPoint(sketch, "E173.visualSharp", {"position": v(19.05, -114.94) * mm});
            skArc(sketch, "E173.filletArc", {"start": v(15.88, -114.94) * mm, "mid": v(18.12, -114) * mm, "end": v(19.05, -111.76) * mm});
            skPoint(sketch, "E174.visualSharp", {"position": v(-184.15, -66.4) * mm});
            skArc(sketch, "E174.filletArc", {"start": v(-182.97, -65.45) * mm, "mid": v(-183.84, -66.55) * mm, "end": v(-184.15, -67.92) * mm});
            skPoint(sketch, "E175.visualSharp", {"position": v(-172.68, -57.15) * mm});
            skArc(sketch, "E175.filletArc", {"start": v(-171.56, -57.15) * mm, "mid": v(-172.62, -57.33) * mm, "end": v(-173.55, -57.85) * mm});
            skPoint(sketch, "E176.visualSharp", {"position": v(-133.98, -57.15) * mm});
            skArc(sketch, "E176.filletArc", {"start": v(-133.83, -57.17) * mm, "mid": v(-133.98, -57.15) * mm, "end": v(-134.14, -57.15) * mm});
            skPoint(sketch, "E177.visualSharp", {"position": v(-184.15, -117.75) * mm});
            skArc(sketch, "E177.filletArc", {"start": v(-184.15, -116.23) * mm, "mid": v(-183.84, -117.6) * mm, "end": v(-182.97, -118.7) * mm});
            skPoint(sketch, "E178.visualSharp", {"position": v(-172.68, -127) * mm});
            skArc(sketch, "E178.filletArc", {"start": v(-173.55, -126.3) * mm, "mid": v(-172.62, -126.82) * mm, "end": v(-171.56, -127) * mm});
            skPoint(sketch, "E179.visualSharp", {"position": v(-133.98, -127) * mm});
            skArc(sketch, "E179.filletArc", {"start": v(-134.14, -127) * mm, "mid": v(-133.98, -127) * mm, "end": v(-133.83, -126.98) * mm});
            skPoint(sketch, "E180.visualSharp", {"position": v(-13.33, -114.93) * mm});
            skArc(sketch, "E180.filletArc", {"start": v(-13.18, -114.93) * mm, "mid": v(-13.33, -114.94) * mm, "end": v(-13.5, -114.95) * mm});
            skPoint(sketch, "E181.visualSharp", {"position": v(-13.33, -69.21) * mm});
            skArc(sketch, "E181.filletArc", {"start": v(-13.5, -69.2) * mm, "mid": v(-13.33, -69.21) * mm, "end": v(-13.18, -69.21) * mm});
            skLineSegment(sketch, "E182.0", {"start": v(-196.85, 54.61) * mm, "end": v(31.75, 54.61) * mm, "construction": true});
            skLineSegment(sketch, "E183.0", {"start": v(-133.35, 133.99) * mm, "end": v(-133.35, -18.41) * mm, "construction": true});
            skLineSegment(sketch, "E184.0", {"start": v(-107.95, 133.99) * mm, "end": v(-107.95, -18.41) * mm, "construction": true});
            skLineSegment(sketch, "E185", {"start": v(-158.75, 54.61) * mm, "end": v(-158.75, 67.31) * mm});
            skLineSegment(sketch, "E186", {"start": v(-155.57, 70.49) * mm, "end": v(-85.72, 70.49) * mm});
            skLineSegment(sketch, "E187", {"start": v(-82.55, 67.31) * mm, "end": v(-82.55, 54.61) * mm});
            skLineSegment(sketch, "E188.MirrorCS", {"start": v(-82.55, 41.91) * mm, "end": v(-82.55, 54.61) * mm});
            skLineSegment(sketch, "E189.MirrorCS", {"start": v(-158.75, 54.61) * mm, "end": v(-158.75, 41.91) * mm});
            skLineSegment(sketch, "E190.MirrorCS", {"start": v(-155.57, 38.74) * mm, "end": v(-85.72, 38.74) * mm});
            skPoint(sketch, "E191.visualSharp", {"position": v(-158.75, 70.49) * mm});
            skArc(sketch, "E191.filletArc", {"start": v(-155.57, 70.49) * mm, "mid": v(-157.82, 69.56) * mm, "end": v(-158.75, 67.31) * mm});
            skPoint(sketch, "E192.visualSharp", {"position": v(-158.75, 38.74) * mm});
            skArc(sketch, "E192.filletArc", {"start": v(-158.75, 41.91) * mm, "mid": v(-157.82, 39.66) * mm, "end": v(-155.57, 38.74) * mm});
            skPoint(sketch, "E193.visualSharp", {"position": v(-82.55, 38.74) * mm});
            skArc(sketch, "E193.filletArc", {"start": v(-85.72, 38.74) * mm, "mid": v(-83.48, 39.66) * mm, "end": v(-82.55, 41.91) * mm});
            skPoint(sketch, "E194.visualSharp", {"position": v(-82.55, 70.49) * mm});
            skArc(sketch, "E194.filletArc", {"start": v(-82.55, 67.31) * mm, "mid": v(-83.48, 69.56) * mm, "end": v(-85.72, 70.49) * mm});
            skSolve(sketch);
        }
        {
            var Q0;
            Q0=qSketchRegion(id+"F2",true);
            extrude(context, id + "F3", {"entities" : qUnion([Q0]), "oppositeDirection" : true, "depth" : 12.7 * mm, "offsetDistance" : 25.4 * mm});
        }
        {
            var Q0;
            Q0=makeQuery(id+"F1.opExtrude","CAP_FACE",FACE,{"disambiguationData":[OSD([sQuery(id+"F0.wireOp",EDGE,"E0.bottom"),sQuery(id+"F0.wireOp",EDGE,"E0.top"),sQuery(id+"F0.wireOp",EDGE,"E0.left"),sQuery(id+"F0.wireOp",EDGE,"E0.right"),sQuery(id+"F0.wireOp",EDGE,"E1.bottom"),sQuery(id+"F0.wireOp",EDGE,"E1.top"),sQuery(id+"F0.wireOp",EDGE,"E1.left"),sQuery(id+"F0.wireOp",EDGE,"E1.right"),sQuery(id+"F0.wireOp",EDGE,"E2.bottom"),sQuery(id+"F0.wireOp",EDGE,"E2.top"),sQuery(id+"F0.wireOp",EDGE,"E2.left"),sQuery(id+"F0.wireOp",EDGE,"E2.right"),sQuery(id+"F0.wireOp",EDGE,"E4"),sQuery(id+"F0.wireOp",EDGE,"E5"),sQuery(id+"F0.wireOp",EDGE,"E6"),sQuery(id+"F0.wireOp",EDGE,"E7"),sQuery(id+"F0.wireOp",EDGE,"E8"),sQuery(id+"F0.wireOp",EDGE,"E9"),sQuery(id+"F0.wireOp",EDGE,"E10.filletArc"),sQuery(id+"F0.wireOp",EDGE,"E11.MirrorCS"),sQuery(id+"F0.wireOp",EDGE,"E12.MirrorCS"),sQuery(id+"F0.wireOp",EDGE,"E13.MirrorCS"),sQuery(id+"F0.wireOp",EDGE,"E15.MirrorCS"),sQuery(id+"F0.wireOp",EDGE,"E16.MirrorCS"),sQuery(id+"F0.wireOp",EDGE,"E17.MirrorCS"),sQuery(id+"F0.wireOp",EDGE,"E18"),sQuery(id+"F0.wireOp",EDGE,"E19.filletArc"),sQuery(id+"F0.wireOp",EDGE,"E20.filletArc"),sQuery(id+"F0.wireOp",EDGE,"E21.filletArc"),sQuery(id+"F0.wireOp",EDGE,"E22.filletArc"),sQuery(id+"F0.wireOp",EDGE,"E23.filletArc"),sQuery(id+"F0.wireOp",EDGE,"E25.filletArc"),sQuery(id+"F0.wireOp",EDGE,"E26.filletArc"),sQuery(id+"F0.wireOp",EDGE,"E27.bottom"),sQuery(id+"F0.wireOp",EDGE,"E27.top"),sQuery(id+"F0.wireOp",EDGE,"E27.left"),sQuery(id+"F0.wireOp",EDGE,"E27.right"),sQuery(id+"F0.wireOp",EDGE,"E28.bottom"),sQuery(id+"F0.wireOp",EDGE,"E28.top"),sQuery(id+"F0.wireOp",EDGE,"E28.right"),sQuery(id+"F0.wireOp",EDGE,"E29.trimOffspring"),sQuery(id+"F0.wireOp",EDGE,"E31.filletArc"),sQuery(id+"F0.wireOp",EDGE,"E32.filletArc"),sQuery(id+"F0.wireOp",EDGE,"E33.filletArc"),sQuery(id+"F0.wireOp",EDGE,"E34.filletArc"),sQuery(id+"F0.wireOp",EDGE,"E35.filletArc"),sQuery(id+"F0.wireOp",EDGE,"E36.filletArc"),sQuery(id+"F0.wireOp",EDGE,"E37.bottom"),sQuery(id+"F0.wireOp",EDGE,"E37.left"),sQuery(id+"F0.wireOp",EDGE,"E37.right"),sQuery(id+"F0.wireOp",EDGE,"E38"),sQuery(id+"F0.wireOp",EDGE,"E48"),sQuery(id+"F0.wireOp",EDGE,"E49"),sQuery(id+"F0.wireOp",EDGE,"E50"),sQuery(id+"F0.wireOp",EDGE,"E51"),sQuery(id+"F0.wireOp",EDGE,"E52"),sQuery(id+"F0.wireOp",EDGE,"E53"),sQuery(id+"F0.wireOp",EDGE,"E54"),sQuery(id+"F0.wireOp",EDGE,"E55"),sQuery(id+"F0.wireOp",EDGE,"E56"),sQuery(id+"F0.wireOp",EDGE,"E57"),sQuery(id+"F0.wireOp",EDGE,"E58.filletArc"),sQuery(id+"F0.wireOp",EDGE,"E59.filletArc"),sQuery(id+"F0.wireOp",EDGE,"E60.filletArc"),sQuery(id+"F0.wireOp",EDGE,"E61.filletArc"),sQuery(id+"F0.wireOp",EDGE,"E62.filletArc"),sQuery(id+"F0.wireOp",EDGE,"E63.filletArc"),sQuery(id+"F0.wireOp",EDGE,"E65.MirrorCS"),sQuery(id+"F0.wireOp",EDGE,"E66.MirrorCS"),sQuery(id+"F0.wireOp",EDGE,"E67"),sQuery(id+"F0.wireOp",EDGE,"E68"),sQuery(id+"F0.wireOp",EDGE,"E69"),sQuery(id+"F0.wireOp",EDGE,"E70.filletArc"),sQuery(id+"F0.wireOp",EDGE,"E71.filletArc"),sQuery(id+"F0.wireOp",EDGE,"E72.filletArc"),sQuery(id+"F0.wireOp",EDGE,"E73.filletArc"),sQuery(id+"F0.wireOp",EDGE,"E74.filletArc"),sQuery(id+"F0.wireOp",EDGE,"E75.filletArc"),sQuery(id+"F0.wireOp",EDGE,"E88"),sQuery(id+"F0.wireOp",EDGE,"E90"),sQuery(id+"F0.wireOp",EDGE,"E91.bottom"),sQuery(id+"F0.wireOp",EDGE,"E91.top"),sQuery(id+"F0.wireOp",EDGE,"E91.left"),sQuery(id+"F0.wireOp",EDGE,"E91.right"),sQuery(id+"F0.wireOp",EDGE,"E95.filletArc"),sQuery(id+"F0.wireOp",EDGE,"E96.filletArc"),sQuery(id+"F0.wireOp",EDGE,"E97.filletArc"),sQuery(id+"F0.wireOp",EDGE,"E98.filletArc")])],"isStart":false});
            var sketch = newSketch(context, id + "F4", { "sketchPlane" : qUnion([Q0])});
            skLineSegment(sketch, "E195.bottom", {"start": v(-203.2, 156.21) * mm, "end": v(203.2, 156.21) * mm});
            skLineSegment(sketch, "E195.top", {"start": v(-203.2, -156.2) * mm, "end": v(203.2, -156.2) * mm});
            skLineSegment(sketch, "E195.left", {"start": v(-222.25, 137.16) * mm, "end": v(-222.25, -137.16) * mm});
            skLineSegment(sketch, "E195.right", {"start": v(222.25, 137.16) * mm, "end": v(222.25, -137.16) * mm});
            skLineSegment(sketch, "E196.bottom", {"start": v(-196.85, -21.59) * mm, "end": v(-196.85, 130.81) * mm, "construction": true});
            skLineSegment(sketch, "E196.top", {"start": v(31.75, -21.59) * mm, "end": v(31.75, 130.81) * mm, "construction": true});
            skLineSegment(sketch, "E196.left", {"start": v(-190.5, -27.94) * mm, "end": v(25.4, -27.94) * mm, "construction": true});
            skLineSegment(sketch, "E196.right", {"start": v(-190.5, 137.16) * mm, "end": v(25.4, 137.16) * mm, "construction": true});
            skLineSegment(sketch, "E197.bottom", {"start": v(124.46, -93.98) * mm, "end": v(154.94, -93.98) * mm});
            skLineSegment(sketch, "E197.top", {"start": v(124.46, -124.46) * mm, "end": v(154.94, -124.46) * mm});
            skLineSegment(sketch, "E197.left", {"start": v(124.46, -93.98) * mm, "end": v(124.46, -124.46) * mm});
            skLineSegment(sketch, "E197.right", {"start": v(154.94, -93.98) * mm, "end": v(154.94, -124.46) * mm});
            skLineSegment(sketch, "E198", {"start": v(142.6, -24.8) * mm, "end": v(186.74, -2.32) * mm, "construction": true});
            skLineSegment(sketch, "E199", {"start": v(142.6, -24.8) * mm, "end": v(155.87, -50.83) * mm});
            skLineSegment(sketch, "E200", {"start": v(164.4, -53.6) * mm, "end": v(177.99, -46.7) * mm});
            skLineSegment(sketch, "E201", {"start": v(177.99, -46.7) * mm, "end": v(190.67, -71.59) * mm});
            skLineSegment(sketch, "E202", {"start": v(190.67, -71.59) * mm, "end": v(195.2, -69.28) * mm});
            skLineSegment(sketch, "E203", {"start": v(160.32, -0.82) * mm, "end": v(180.68, 9.56) * mm});
            skLineSegment(sketch, "E204", {"start": v(180.68, 9.56) * mm, "end": v(186.74, -2.32) * mm});
            skPoint(sketch, "E205.visualSharp", {"position": v(158.75, -56.5) * mm});
            skArc(sketch, "E205.filletArc", {"start": v(155.87, -50.83) * mm, "mid": v(159.56, -54) * mm, "end": v(164.4, -53.6) * mm});
            skArc(sketch, "E206.MirrorCS", {"start": v(129.35, 1.22) * mm, "mid": v(128.96, 6.06) * mm, "end": v(132.12, 9.76) * mm});
            skLineSegment(sketch, "E207.MirrorCS", {"start": v(145.7, 16.68) * mm, "end": v(133.02, 41.57) * mm});
            skLineSegment(sketch, "E208.MirrorCS", {"start": v(132.12, 9.76) * mm, "end": v(145.7, 16.68) * mm});
            skPoint(sketch, "E209.MirrorP", {"position": v(126.46, 6.88) * mm});
            skLineSegment(sketch, "E210.MirrorCS", {"start": v(172.42, -24.58) * mm, "end": v(192.8, -14.2) * mm});
            skLineSegment(sketch, "E211.MirrorCS", {"start": v(142.6, -24.8) * mm, "end": v(129.35, 1.22) * mm});
            skLineSegment(sketch, "E212.MirrorCS", {"start": v(192.8, -14.2) * mm, "end": v(186.74, -2.32) * mm});
            skLineSegment(sketch, "E213", {"start": v(172.42, -24.58) * mm, "end": v(195.2, -69.28) * mm});
            skPoint(sketch, "E214.visualSharp", {"position": v(-222.25, 156.21) * mm});
            skArc(sketch, "E214.filletArc", {"start": v(-203.2, 156.21) * mm, "mid": v(-216.67, 150.63) * mm, "end": v(-222.25, 137.16) * mm});
            skPoint(sketch, "E215.visualSharp", {"position": v(222.25, 156.21) * mm});
            skArc(sketch, "E215.filletArc", {"start": v(222.25, 137.16) * mm, "mid": v(216.67, 150.63) * mm, "end": v(203.2, 156.21) * mm});
            skPoint(sketch, "E216.visualSharp", {"position": v(222.25, -156.2) * mm});
            skArc(sketch, "E216.filletArc", {"start": v(203.2, -156.2) * mm, "mid": v(216.67, -150.63) * mm, "end": v(222.25, -137.16) * mm});
            skPoint(sketch, "E217.visualSharp", {"position": v(-222.25, -156.2) * mm});
            skArc(sketch, "E217.filletArc", {"start": v(-222.25, -137.16) * mm, "mid": v(-216.67, -150.63) * mm, "end": v(-203.2, -156.21) * mm});
            skPoint(sketch, "E218.visualSharp", {"position": v(-196.85, -27.94) * mm});
            skArc(sketch, "E218.filletArc", {"start": v(-196.85, -21.59) * mm, "mid": v(-195, -26.08) * mm, "end": v(-190.5, -27.94) * mm, "construction": true});
            skPoint(sketch, "E219.visualSharp", {"position": v(31.75, -27.94) * mm});
            skArc(sketch, "E219.filletArc", {"start": v(25.4, -27.94) * mm, "mid": v(29.9, -26.08) * mm, "end": v(31.75, -21.59) * mm, "construction": true});
            skPoint(sketch, "E220.visualSharp", {"position": v(-196.85, 137.16) * mm});
            skArc(sketch, "E220.filletArc", {"start": v(-190.5, 137.16) * mm, "mid": v(-195, 135.3) * mm, "end": v(-196.85, 130.81) * mm, "construction": true});
            skPoint(sketch, "E221.visualSharp", {"position": v(31.75, 137.16) * mm});
            skArc(sketch, "E221.filletArc", {"start": v(31.75, 130.81) * mm, "mid": v(29.9, 135.3) * mm, "end": v(25.4, 137.16) * mm, "construction": true});
            skLineSegment(sketch, "E222.bottom", {"start": v(63.5, 88.9) * mm, "end": v(63.5, 124.46) * mm});
            skLineSegment(sketch, "E222.top", {"start": v(196.85, 88.9) * mm, "end": v(196.85, 112.08) * mm});
            skLineSegment(sketch, "E222.left", {"start": v(69.85, 82.55) * mm, "end": v(146.05, 82.55) * mm});
            skLineSegment(sketch, "E222.right", {"start": v(69.85, 130.81) * mm, "end": v(190.5, 130.81) * mm});
            skLineSegment(sketch, "E223.bottom", {"start": v(147.32, 81.28) * mm, "end": v(147.32, 63.5) * mm});
            skLineSegment(sketch, "E223.top", {"start": v(166.37, 81.28) * mm, "end": v(166.37, 63.5) * mm});
            skLineSegment(sketch, "E223.right", {"start": v(153.67, 57.15) * mm, "end": v(160.02, 57.15) * mm});
            skLineSegment(sketch, "E224.trimOffspring", {"start": v(167.64, 82.55) * mm, "end": v(190.5, 82.55) * mm});
            skLineSegment(sketch, "E225", {"start": v(147.32, 82.55) * mm, "end": v(166.37, 82.55) * mm, "construction": true});
            skPoint(sketch, "E226.visualSharp", {"position": v(63.5, 82.55) * mm});
            skArc(sketch, "E226.filletArc", {"start": v(63.5, 88.9) * mm, "mid": v(65.36, 84.4) * mm, "end": v(69.85, 82.55) * mm});
            skPoint(sketch, "E227.visualSharp", {"position": v(196.85, 82.55) * mm});
            skArc(sketch, "E227.filletArc", {"start": v(190.5, 82.55) * mm, "mid": v(195, 84.4) * mm, "end": v(196.85, 88.9) * mm});
            skPoint(sketch, "E228.visualSharp", {"position": v(196.85, 130.81) * mm});
            skArc(sketch, "E228.filletArc", {"start": v(196.85, 124.46) * mm, "mid": v(195, 128.95) * mm, "end": v(190.5, 130.81) * mm});
            skPoint(sketch, "E229.visualSharp", {"position": v(63.5, 130.81) * mm});
            skArc(sketch, "E229.filletArc", {"start": v(69.85, 130.81) * mm, "mid": v(65.36, 128.95) * mm, "end": v(63.5, 124.46) * mm});
            skPoint(sketch, "E230.visualSharp", {"position": v(147.32, 57.15) * mm});
            skArc(sketch, "E230.filletArc", {"start": v(147.32, 63.5) * mm, "mid": v(149.18, 59) * mm, "end": v(153.67, 57.15) * mm});
            skPoint(sketch, "E231.visualSharp", {"position": v(166.37, 57.15) * mm});
            skArc(sketch, "E231.filletArc", {"start": v(160.02, 57.15) * mm, "mid": v(164.51, 59) * mm, "end": v(166.37, 63.5) * mm});
            skLineSegment(sketch, "E232.bottom", {"start": v(173.74, -91.44) * mm, "end": v(196.85, -91.44) * mm, "construction": true});
            skLineSegment(sketch, "E232.left", {"start": v(173.74, -91.44) * mm, "end": v(173.74, -116.84) * mm});
            skLineSegment(sketch, "E232.right", {"start": v(196.85, -91.44) * mm, "end": v(196.85, -116.84) * mm});
            skArc(sketch, "E233", {"start": v(173.74, -116.84) * mm, "mid": v(185.3, -128.4) * mm, "end": v(196.85, -116.84) * mm});
            skLineSegment(sketch, "E234.bottom", {"start": v(-196.85, -139.7) * mm, "end": v(-196.85, -44.45) * mm, "construction": true});
            skLineSegment(sketch, "E234.top", {"start": v(31.75, -139.7) * mm, "end": v(31.75, -44.45) * mm, "construction": true});
            skLineSegment(sketch, "E234.left", {"start": v(-196.85, -139.7) * mm, "end": v(31.75, -139.7) * mm, "construction": true});
            skLineSegment(sketch, "E234.right", {"start": v(-196.85, -44.45) * mm, "end": v(31.75, -44.45) * mm, "construction": true});
            skLineSegment(sketch, "E235", {"start": v(-196.85, -92.07) * mm, "end": v(31.75, -92.07) * mm, "construction": true});
            skLineSegment(sketch, "E236", {"start": v(-196.85, -123.82) * mm, "end": v(31.75, -123.82) * mm, "construction": true});
            skLineSegment(sketch, "E237.MirrorCS", {"start": v(-196.85, -60.32) * mm, "end": v(31.75, -60.32) * mm, "construction": true});
            skLineSegment(sketch, "E238", {"start": v(-196.85, -127.63) * mm, "end": v(31.75, -127.63) * mm, "construction": true});
            skLineSegment(sketch, "E239.MirrorCS", {"start": v(-196.85, -56.51) * mm, "end": v(31.75, -56.51) * mm, "construction": true});
            skLineSegment(sketch, "E240", {"start": v(-177.16, -139.7) * mm, "end": v(-177.16, -44.45) * mm, "construction": true});
            skLineSegment(sketch, "E241", {"start": v(-133.35, -139.7) * mm, "end": v(-133.35, -44.45) * mm, "construction": true});
            skLineSegment(sketch, "E242", {"start": v(-12.7, -139.7) * mm, "end": v(-12.7, -44.45) * mm, "construction": true});
            skLineSegment(sketch, "E243", {"start": v(-196.85, -120.79) * mm, "end": v(-196.85, -63.36) * mm});
            skLineSegment(sketch, "E244", {"start": v(-194.49, -58.42) * mm, "end": v(-178.9, -45.86) * mm});
            skLineSegment(sketch, "E245", {"start": v(-174.92, -44.45) * mm, "end": v(-133.35, -44.45) * mm});
            skLineSegment(sketch, "E246", {"start": v(-133.35, -44.45) * mm, "end": v(-12.7, -56.51) * mm});
            skLineSegment(sketch, "E247", {"start": v(-12.7, -56.51) * mm, "end": v(25.4, -56.51) * mm});
            skLineSegment(sketch, "E248", {"start": v(31.75, -62.86) * mm, "end": v(31.75, -121.28) * mm});
            skLineSegment(sketch, "E249", {"start": v(25.4, -127.63) * mm, "end": v(-12.7, -127.63) * mm});
            skLineSegment(sketch, "E250", {"start": v(-12.7, -127.63) * mm, "end": v(-133.35, -139.7) * mm});
            skLineSegment(sketch, "E251", {"start": v(-133.35, -139.7) * mm, "end": v(-174.92, -139.7) * mm});
            skLineSegment(sketch, "E252", {"start": v(-178.9, -138.3) * mm, "end": v(-194.49, -125.73) * mm});
            skPoint(sketch, "E253.visualSharp", {"position": v(31.75, -127.63) * mm});
            skArc(sketch, "E253.filletArc", {"start": v(25.4, -127.63) * mm, "mid": v(29.9, -125.78) * mm, "end": v(31.75, -121.28) * mm});
            skPoint(sketch, "E254.visualSharp", {"position": v(31.75, -56.51) * mm});
            skArc(sketch, "E254.filletArc", {"start": v(31.75, -62.86) * mm, "mid": v(29.9, -58.37) * mm, "end": v(25.4, -56.51) * mm});
            skPoint(sketch, "E255.visualSharp", {"position": v(-196.85, -123.82) * mm});
            skArc(sketch, "E255.filletArc", {"start": v(-196.85, -120.79) * mm, "mid": v(-196.23, -123.53) * mm, "end": v(-194.49, -125.73) * mm});
            skPoint(sketch, "E256.visualSharp", {"position": v(-177.16, -139.7) * mm});
            skArc(sketch, "E256.filletArc", {"start": v(-178.9, -138.3) * mm, "mid": v(-177.04, -139.34) * mm, "end": v(-174.92, -139.7) * mm});
            skPoint(sketch, "E257.visualSharp", {"position": v(-196.85, -60.32) * mm});
            skArc(sketch, "E257.filletArc", {"start": v(-194.49, -58.42) * mm, "mid": v(-196.23, -60.62) * mm, "end": v(-196.85, -63.36) * mm});
            skPoint(sketch, "E258.visualSharp", {"position": v(-177.16, -44.45) * mm});
            skArc(sketch, "E258.filletArc", {"start": v(-174.92, -44.45) * mm, "mid": v(-177.04, -44.81) * mm, "end": v(-178.9, -45.86) * mm});
            skLineSegment(sketch, "E259", {"start": v(173.74, -116.84) * mm, "end": v(196.85, -116.84) * mm, "construction": true});
            skLineSegment(sketch, "E260.MirrorCS", {"start": v(160.32, -0.82) * mm, "end": v(137.54, 43.88) * mm});
            skLineSegment(sketch, "E261.MirrorCS", {"start": v(133.02, 41.57) * mm, "end": v(137.54, 43.88) * mm});
            skLineSegment(sketch, "E262", {"start": v(198.12, 122.87) * mm, "end": v(198.76, 122.87) * mm});
            skLineSegment(sketch, "E263", {"start": v(200.03, 121.6) * mm, "end": v(200.03, 114.62) * mm});
            skLineSegment(sketch, "E264", {"start": v(198.76, 113.35) * mm, "end": v(198.12, 113.35) * mm});
            skPoint(sketch, "E265.visualSharp", {"position": v(166.37, 82.55) * mm});
            skArc(sketch, "E265.filletArc", {"start": v(167.64, 82.55) * mm, "mid": v(166.74, 82.18) * mm, "end": v(166.37, 81.28) * mm});
            skPoint(sketch, "E266.visualSharp", {"position": v(147.32, 82.55) * mm});
            skArc(sketch, "E266.filletArc", {"start": v(147.32, 81.28) * mm, "mid": v(146.95, 82.18) * mm, "end": v(146.05, 82.55) * mm});
            skPoint(sketch, "E267.visualSharp", {"position": v(200.03, 113.35) * mm});
            skArc(sketch, "E267.filletArc", {"start": v(198.76, 113.35) * mm, "mid": v(199.65, 113.72) * mm, "end": v(200.03, 114.62) * mm});
            skPoint(sketch, "E268.visualSharp", {"position": v(200.03, 122.87) * mm});
            skArc(sketch, "E268.filletArc", {"start": v(200.03, 121.6) * mm, "mid": v(199.65, 122.5) * mm, "end": v(198.76, 122.87) * mm});
            skPoint(sketch, "E269.visualSharp", {"position": v(196.85, 122.87) * mm});
            skArc(sketch, "E269.filletArc", {"start": v(196.85, 124.13) * mm, "mid": v(197.23, 123.24) * mm, "end": v(198.12, 122.87) * mm});
            skPoint(sketch, "E270.visualSharp", {"position": v(196.85, 113.35) * mm});
            skArc(sketch, "E270.filletArc", {"start": v(198.12, 113.35) * mm, "mid": v(197.22, 112.98) * mm, "end": v(196.85, 112.08) * mm});
            skLineSegment(sketch, "E271", {"start": v(-196.85, 54.61) * mm, "end": v(31.75, 54.61) * mm, "construction": true});
            skLineSegment(sketch, "E272", {"start": v(-82.55, -27.94) * mm, "end": v(-82.55, 137.16) * mm, "construction": true});
            skLineSegment(sketch, "E273", {"start": v(0, 156.21) * mm, "end": v(0, -156.2) * mm, "construction": true});
            skLineSegment(sketch, "E274", {"start": v(-222.25, 0) * mm, "end": v(222.25, 0) * mm, "construction": true});
            skPoint(sketch, "E275", {"position": v(0, 0) * mm});
            skPoint(sketch, "E276", {"position": v(-82.55, 54.61) * mm});
            skPoint(sketch, "E277", {"position": v(-133.35, -92.07) * mm});
            skLineSegment(sketch, "E278", {"start": v(63.5, 106.68) * mm, "end": v(196.85, 106.68) * mm, "construction": true});
            skLineSegment(sketch, "E279", {"start": v(130.18, 130.81) * mm, "end": v(130.18, 82.55) * mm, "construction": true});
            skPoint(sketch, "E280", {"position": v(130.18, 106.68) * mm});
            skLineSegment(sketch, "E281", {"start": v(172.42, -24.58) * mm, "end": v(160.32, -0.82) * mm, "construction": true});
            skPoint(sketch, "E282", {"position": v(166.37, -12.7) * mm});
            skLineSegment(sketch, "E283", {"start": v(196.85, 124.46) * mm, "end": v(196.85, 124.13) * mm});
            skLineSegment(sketch, "E284", {"start": v(196.85, 124.13) * mm, "end": v(196.85, 112.08) * mm, "construction": true});
            skArc(sketch, "E285", {"start": v(31.75, -21.59) * mm, "mid": v(29.9, -26.08) * mm, "end": v(25.4, -27.94) * mm, "construction": true});
            skLineSegment(sketch, "E286.bottom", {"start": v(107.95, -137.16) * mm, "end": v(57.15, -137.16) * mm});
            skLineSegment(sketch, "E286.top", {"start": v(107.95, 66.04) * mm, "end": v(57.15, 66.04) * mm});
            skLineSegment(sketch, "E286.left", {"start": v(114.3, -130.8) * mm, "end": v(114.3, 59.69) * mm});
            skLineSegment(sketch, "E286.right", {"start": v(50.8, -130.8) * mm, "end": v(50.8, 59.69) * mm});
            skLineSegment(sketch, "E287", {"start": v(82.55, -137.16) * mm, "end": v(82.55, 66.04) * mm, "construction": true});
            skLineSegment(sketch, "E288", {"start": v(114.3, -35.56) * mm, "end": v(50.8, -35.56) * mm, "construction": true});
            skPoint(sketch, "E289", {"position": v(82.55, -35.56) * mm});
            skPoint(sketch, "E290.visualSharp", {"position": v(114.3, -137.16) * mm});
            skArc(sketch, "E290.filletArc", {"start": v(107.95, -137.16) * mm, "mid": v(112.44, -135.3) * mm, "end": v(114.3, -130.8) * mm});
            skPoint(sketch, "E291.visualSharp", {"position": v(50.8, -137.16) * mm});
            skArc(sketch, "E291.filletArc", {"start": v(50.8, -130.8) * mm, "mid": v(52.66, -135.3) * mm, "end": v(57.15, -137.16) * mm});
            skPoint(sketch, "E292.visualSharp", {"position": v(50.8, 66.04) * mm});
            skArc(sketch, "E292.filletArc", {"start": v(57.15, 66.04) * mm, "mid": v(52.66, 64.18) * mm, "end": v(50.8, 59.69) * mm});
            skPoint(sketch, "E293.visualSharp", {"position": v(114.3, 66.04) * mm});
            skArc(sketch, "E293.filletArc", {"start": v(114.3, 59.69) * mm, "mid": v(112.44, 64.18) * mm, "end": v(107.95, 66.04) * mm});
            skLineSegment(sketch, "E294", {"start": v(185.3, -91.44) * mm, "end": v(185.3, -128.4) * mm, "construction": true});
            skLineSegment(sketch, "E295.bottom", {"start": v(-193.68, 143.5) * mm, "end": v(-193.68, 143.5) * mm});
            skLineSegment(sketch, "E295.top", {"start": v(-193.68, -34.3) * mm, "end": v(0, -34.3) * mm});
            skLineSegment(sketch, "E295.left", {"start": v(-206.38, 130.8) * mm, "end": v(-206.38, 130.8) * mm});
            skLineSegment(sketch, "E295.right", {"start": v(41.28, 130.8) * mm, "end": v(41.28, 121.33) * mm, "construction": true});
            skPoint(sketch, "E296.visualSharp", {"position": v(-206.38, 143.5) * mm});
            skArc(sketch, "E296.filletArc", {"start": v(-193.68, 143.5) * mm, "mid": v(-202.66, 139.8) * mm, "end": v(-206.38, 130.8) * mm});
            skPoint(sketch, "E297.visualSharp", {"position": v(41.28, 143.5) * mm});
            skArc(sketch, "E297.filletArc", {"start": v(41.28, 130.8) * mm, "mid": v(37.56, 139.8) * mm, "end": v(28.58, 143.51) * mm});
            skPoint(sketch, "E298.visualSharp", {"position": v(41.27, -34.3) * mm});
            skArc(sketch, "E298.filletArc", {"start": v(28.57, -34.3) * mm, "mid": v(37.56, -30.57) * mm, "end": v(41.27, -21.6) * mm});
            skPoint(sketch, "E299.visualSharp", {"position": v(-206.38, -34.3) * mm});
            skArc(sketch, "E299.filletArc", {"start": v(-206.38, -21.6) * mm, "mid": v(-202.66, -30.57) * mm, "end": v(-193.68, -34.3) * mm});
            skArc(sketch, "E300", {"start": v(-206.38, 62.23) * mm, "mid": v(-214, 54.6) * mm, "end": v(-206.38, 46.99) * mm});
            skLineSegment(sketch, "E301", {"start": v(-206.38, 62.23) * mm, "end": v(-206.38, 46.99) * mm, "construction": true});
            skLineSegment(sketch, "E302", {"start": v(-206.38, 46.99) * mm, "end": v(-206.38, -21.6) * mm});
            skArc(sketch, "E303", {"start": v(124.46, -93.98) * mm, "mid": v(139.7, -78.74) * mm, "end": v(154.94, -93.98) * mm});
            skArc(sketch, "E304", {"start": v(154.94, -124.46) * mm, "mid": v(139.7, -139.7) * mm, "end": v(124.46, -124.46) * mm});
            skArc(sketch, "E305", {"start": v(173.74, -91.44) * mm, "mid": v(185.3, -79.88) * mm, "end": v(196.85, -91.44) * mm});
            skLineSegment(sketch, "E306", {"start": v(-193.68, 111.76) * mm, "end": v(0, 111.76) * mm});
            skLineSegment(sketch, "E307", {"start": v(12.7, 99.06) * mm, "end": v(12.7, -21.6) * mm});
            skPoint(sketch, "E308.visualSharp", {"position": v(12.7, 111.76) * mm});
            skArc(sketch, "E308.filletArc", {"start": v(12.7, 99.06) * mm, "mid": v(8.98, 108.04) * mm, "end": v(0, 111.76) * mm});
            skLineSegment(sketch, "E309", {"start": v(-206.38, 99.06) * mm, "end": v(-206.38, 62.23) * mm});
            skLineSegment(sketch, "E310", {"start": v(12.7, -34.3) * mm, "end": v(19, -34.3) * mm});
            skPoint(sketch, "E311.visualSharp", {"position": v(-206.38, 111.76) * mm});
            skArc(sketch, "E311.filletArc", {"start": v(-193.68, 111.76) * mm, "mid": v(-202.66, 108.04) * mm, "end": v(-206.38, 99.06) * mm});
            skPoint(sketch, "E312.visualSharp", {"position": v(12.7, -34.29) * mm});
            skArc(sketch, "E312.filletArc", {"start": v(0, -34.3) * mm, "mid": v(8.98, -30.57) * mm, "end": v(12.7, -21.6) * mm});
            skLineSegment(sketch, "E313", {"start": v(-206.38, 111.76) * mm, "end": v(-206.38, 110.32) * mm});
            skLineSegment(sketch, "E314", {"start": v(12.7, -34.3) * mm, "end": v(11.1, -34.3) * mm});
            skLineSegment(sketch, "E315", {"start": v(173.74, -106.68) * mm, "end": v(196.85, -106.68) * mm});
            skPoint(sketch, "E316", {"position": v(-206.38, 110.3) * mm});
            skPoint(sketch, "E317", {"position": v(-206.38, 121.28) * mm});
            skPoint(sketch, "E318", {"position": v(-184.15, 143.5) * mm});
            skPoint(sketch, "E319", {"position": v(-158.75, 143.5) * mm});
            skPoint(sketch, "E320", {"position": v(-149.23, 143.5) * mm});
            skPoint(sketch, "E321", {"position": v(-123.83, 143.5) * mm});
            skPoint(sketch, "E322", {"position": v(-114.3, 143.5) * mm});
            skPoint(sketch, "E323", {"position": v(-88.9, 143.5) * mm});
            skPoint(sketch, "E324", {"position": v(-79.38, 143.5) * mm});
            skPoint(sketch, "E325", {"position": v(-53.97, 143.5) * mm});
            skPoint(sketch, "E326", {"position": v(-44.45, 143.5) * mm});
            skPoint(sketch, "E327", {"position": v(-19.05, 143.5) * mm});
            skPoint(sketch, "E328", {"position": v(-9.52, 143.5) * mm});
            skPoint(sketch, "E329", {"position": v(19.05, 143.5) * mm});
            skPoint(sketch, "E330", {"position": v(41.28, 121.28) * mm});
            skPoint(sketch, "E331", {"position": v(41.28, 95.88) * mm});
            skPoint(sketch, "E332", {"position": v(41.28, 86.36) * mm});
            skPoint(sketch, "E333", {"position": v(41.27, 60.96) * mm});
            skPoint(sketch, "E334", {"position": v(41.28, 51.43) * mm});
            skPoint(sketch, "E335", {"position": v(41.28, 54.6) * mm});
            skPoint(sketch, "E336", {"position": v(41.27, 26.03) * mm});
            skPoint(sketch, "E337", {"position": v(41.27, 16.5) * mm});
            skPoint(sketch, "E338", {"position": v(41.27, -12.07) * mm});
            skPoint(sketch, "E339", {"position": v(19.05, -34.3) * mm});
            skPoint(sketch, "E340", {"position": v(11.23, -34.3) * mm});
            skPoint(sketch, "E341", {"position": v(-206.38, 103.96) * mm});
            skPoint(sketch, "E342", {"position": v(4.88, -34.3) * mm});
            skLineSegment(sketch, "E343", {"start": v(-206.38, 110.32) * mm, "end": v(-206.38, 103.95) * mm, "construction": true});
            skLineSegment(sketch, "E344", {"start": v(-206.38, 103.95) * mm, "end": v(-206.38, 99.06) * mm});
            skLineSegment(sketch, "E345", {"start": v(-206.38, 130.8) * mm, "end": v(-206.38, 121.28) * mm, "construction": true});
            skLineSegment(sketch, "E346", {"start": v(-193.68, 143.5) * mm, "end": v(-184.33, 143.5) * mm, "construction": true});
            skLineSegment(sketch, "E347", {"start": v(-184.33, 143.5) * mm, "end": v(-158.7, 143.5) * mm});
            skLineSegment(sketch, "E348", {"start": v(-149.24, 143.5) * mm, "end": v(-123.98, 143.5) * mm});
            skLineSegment(sketch, "E349", {"start": v(-123.98, 143.5) * mm, "end": v(-114.26, 143.5) * mm, "construction": true});
            skLineSegment(sketch, "E350", {"start": v(-88.83, 143.5) * mm, "end": v(-79.25, 143.5) * mm, "construction": true});
            skLineSegment(sketch, "E351", {"start": v(-53.9, 143.5) * mm, "end": v(-44.37, 143.5) * mm, "construction": true});
            skLineSegment(sketch, "E352", {"start": v(-18.87, 143.5) * mm, "end": v(-9.66, 143.5) * mm, "construction": true});
            skLineSegment(sketch, "E353", {"start": v(-9.66, 143.5) * mm, "end": v(19.21, 143.5) * mm});
            skLineSegment(sketch, "E354", {"start": v(41.28, 121.33) * mm, "end": v(41.28, 96.14) * mm});
            skLineSegment(sketch, "E355", {"start": v(41.28, 96.14) * mm, "end": v(41.28, 86.93) * mm, "construction": true});
            skLineSegment(sketch, "E356", {"start": v(41.28, 86.93) * mm, "end": v(41.28, 61.3) * mm});
            skLineSegment(sketch, "E357", {"start": v(41.28, 61.3) * mm, "end": v(41.28, 51.84) * mm, "construction": true});
            skLineSegment(sketch, "E358", {"start": v(41.28, 51.84) * mm, "end": v(41.27, 26.06) * mm});
            skLineSegment(sketch, "E359", {"start": v(41.27, 26.06) * mm, "end": v(41.27, 16.63) * mm, "construction": true});
            skLineSegment(sketch, "E360", {"start": v(41.27, 16.63) * mm, "end": v(41.27, -11.65) * mm});
            skLineSegment(sketch, "E361", {"start": v(41.27, -11.65) * mm, "end": v(41.27, -21.6) * mm, "construction": true});
            skLineSegment(sketch, "E362", {"start": v(19, -34.3) * mm, "end": v(28.57, -34.3) * mm, "construction": true});
            skLineSegment(sketch, "E363", {"start": v(4.85, -34.3) * mm, "end": v(0, -34.3) * mm});
            skLineSegment(sketch, "E364", {"start": v(11.1, -34.3) * mm, "end": v(4.85, -34.3) * mm, "construction": true});
            skLineSegment(sketch, "E365", {"start": v(-158.7, 143.5) * mm, "end": v(-149.24, 143.5) * mm, "construction": true});
            skLineSegment(sketch, "E366", {"start": v(-114.26, 143.5) * mm, "end": v(-88.83, 143.5) * mm});
            skLineSegment(sketch, "E367", {"start": v(-79.25, 143.5) * mm, "end": v(-53.9, 143.5) * mm});
            skLineSegment(sketch, "E368", {"start": v(-44.37, 143.5) * mm, "end": v(-18.87, 143.5) * mm});
            skLineSegment(sketch, "E369", {"start": v(19.21, 143.5) * mm, "end": v(28.58, 143.5) * mm, "construction": true});
            skLineSegment(sketch, "E370", {"start": v(-206.38, 121.28) * mm, "end": v(-206.38, 111.76) * mm});
            skSolve(sketch);
        }
        {
            var Q0;
            Q0=qSketchRegion(id+"F4",true);
            extrude(context, id + "F5", {"entities" : qUnion([Q0]), "depth" : 12.7 * mm, "offsetDistance" : 25.4 * mm});
        }
    });
